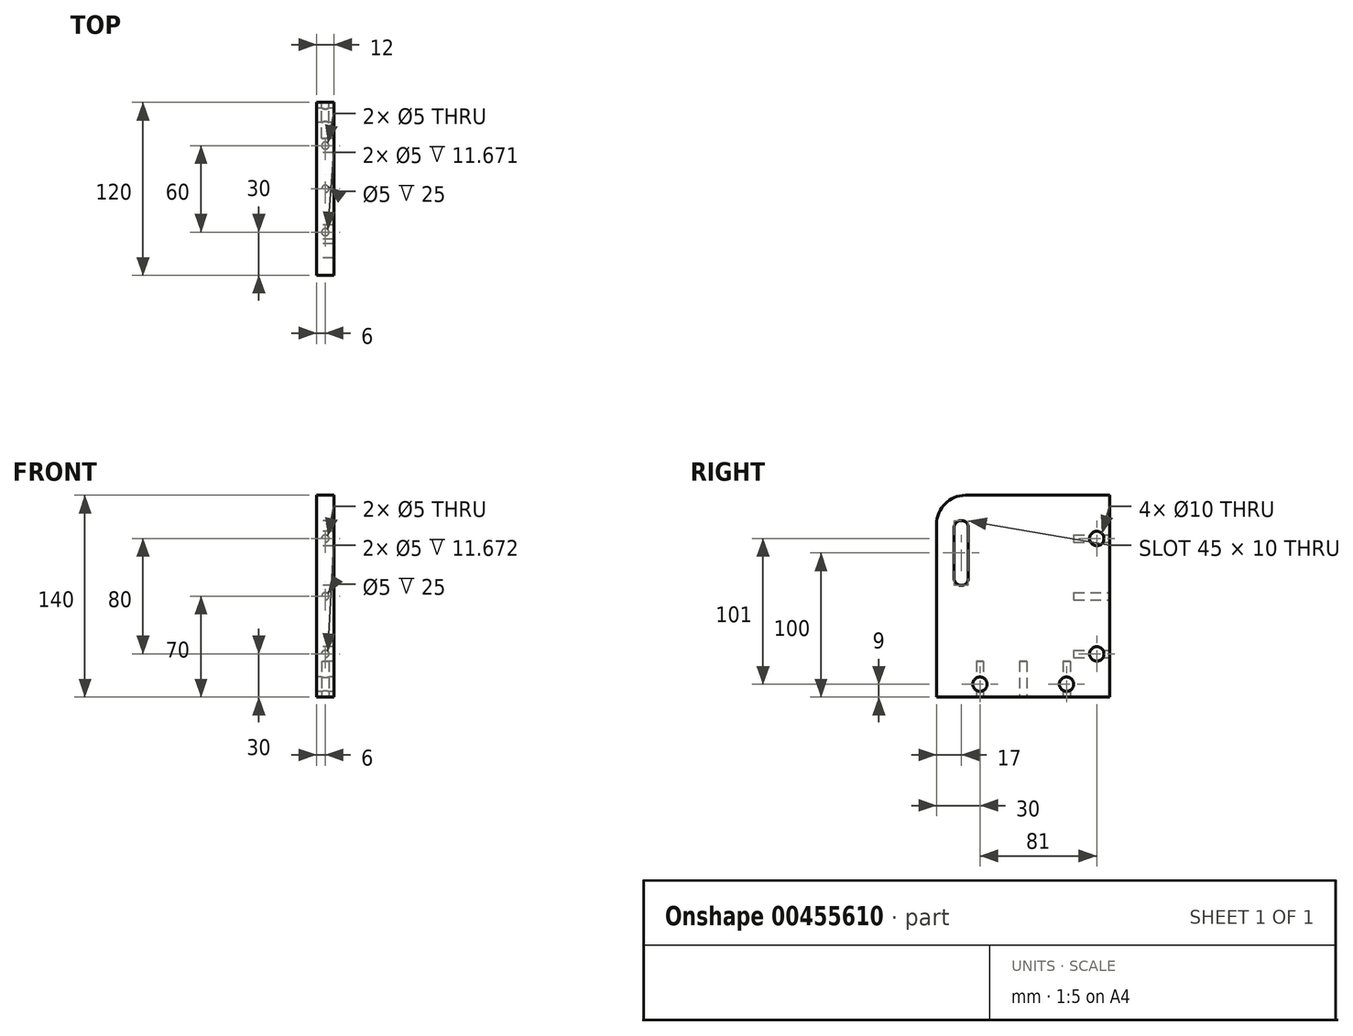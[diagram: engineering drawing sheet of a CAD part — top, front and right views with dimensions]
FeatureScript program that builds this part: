
annotation { "Feature Type Name" : "Feature", "Feature Type Description" : "" }
export const myFeature = defineFeature(function(context is Context, id is Id, definition is map)
    precondition{}
    {
        {
            var Q0;
            Q0=qCreatedBy(makeId("Right.planeOp"),FACE);
            var sketch = newSketch(context, id + "F0", { "sketchPlane" : qUnion([Q0])});
            skLineSegment(sketch, "E0.bottom", {"start": v(-60, 0) * mm, "end": v(60, 0) * mm});
            skLineSegment(sketch, "E0.top", {"start": v(-40, 140) * mm, "end": v(60, 140) * mm});
            skLineSegment(sketch, "E0.left", {"start": v(-60, 0) * mm, "end": v(-60, 120) * mm});
            skLineSegment(sketch, "E0.right", {"start": v(60, 0) * mm, "end": v(60, 140) * mm});
            skLineSegment(sketch, "E1.0", {"start": v(-60, 9) * mm, "end": v(60, 9) * mm, "construction": true});
            skLineSegment(sketch, "E2.0", {"start": v(51, 0) * mm, "end": v(51, 140) * mm, "construction": true});
            skCircle(sketch, "E3", {"center": v(51, 110) * mm, "radius": 5 * mm});
            skCircle(sketch, "E4", {"center": v(51, 30) * mm, "radius": 5 * mm});
            skCircle(sketch, "E5", {"center": v(-30, 9) * mm, "radius": 5 * mm});
            skCircle(sketch, "E6", {"center": v(30, 9) * mm, "radius": 5 * mm});
            skPoint(sketch, "E7.visualSharp", {"position": v(-60, 140) * mm});
            skArc(sketch, "E7.filletArc", {"start": v(-40, 140) * mm, "mid": v(-54.14, 134.14) * mm, "end": v(-60, 120) * mm});
            skLineSegment(sketch, "E8.bottom", {"start": v(-43, 122.5) * mm, "end": v(-43, 122.5) * mm});
            skLineSegment(sketch, "E8.top", {"start": v(-43, 77.5) * mm, "end": v(-43, 77.5) * mm});
            skLineSegment(sketch, "E8.left", {"start": v(-48, 117.5) * mm, "end": v(-48, 82.5) * mm});
            skLineSegment(sketch, "E8.right", {"start": v(-38, 117.5) * mm, "end": v(-38, 82.5) * mm});
            skPoint(sketch, "E9.visualSharp", {"position": v(-48, 122.5) * mm});
            skArc(sketch, "E9.filletArc", {"start": v(-43, 122.5) * mm, "mid": v(-46.54, 121.04) * mm, "end": v(-48, 117.5) * mm});
            skPoint(sketch, "E10.visualSharp", {"position": v(-38, 122.5) * mm});
            skArc(sketch, "E10.filletArc", {"start": v(-38, 117.5) * mm, "mid": v(-39.46, 121.04) * mm, "end": v(-43, 122.5) * mm});
            skPoint(sketch, "E11.visualSharp", {"position": v(-38, 77.5) * mm});
            skArc(sketch, "E11.filletArc", {"start": v(-43, 77.5) * mm, "mid": v(-39.46, 78.96) * mm, "end": v(-38, 82.5) * mm});
            skPoint(sketch, "E12.visualSharp", {"position": v(-48, 77.5) * mm});
            skArc(sketch, "E12.filletArc", {"start": v(-48, 82.5) * mm, "mid": v(-46.54, 78.96) * mm, "end": v(-43, 77.5) * mm});
            skPoint(sketch, "E13", {"position": v(-48, 100) * mm});
            skSolve(sketch);
        }
        {
            var Q0;
            Q0 = qSketchRegion(id + "F0", true);
            extrude(context, id + "F1", {"entities" : qUnion([Q0]), "depth" : 12 * mm});
        }
        {
            var Q0;
            Q0=makeQuery(id+"F1.opExtrude","SWEPT_FACE",FACE,{"disambiguationData":[OSD([sQuery(id+"F0.wireOp",EDGE,"E0.bottom")])]});
            var sketch = newSketch(context, id + "F2", { "sketchPlane" : qUnion([Q0])});
            skLineSegment(sketch, "E14", {"start": v(6, 60) * mm, "end": v(6, -60) * mm, "construction": true});
            skCircle(sketch, "E15", {"center": v(6, 0) * mm, "radius": 2.5 * mm});
            skCircle(sketch, "E16", {"center": v(6, 30) * mm, "radius": 2.5 * mm});
            skCircle(sketch, "E17", {"center": v(6, -30) * mm, "radius": 2.5 * mm});
            skSolve(sketch);
        }
        {
            var Q0;
            Q0 = qSketchRegion(id + "F2", true);
            extrude(context, id + "F3", {"entities" : qUnion([Q0]), "operationType" : NewBodyOperationType.REMOVE, "oppositeDirection" : true, "depth" : 25 * mm});
        }
        {
            var Q0;
            Q0=makeQuery(id+"F1.opExtrude","SWEPT_FACE",FACE,{"disambiguationData":[OSD([sQuery(id+"F0.wireOp",EDGE,"E0.right")])]});
            var sketch = newSketch(context, id + "F4", { "sketchPlane" : qUnion([Q0])});
            skLineSegment(sketch, "E18", {"start": v(-6, 0) * mm, "end": v(-6, 140) * mm, "construction": true});
            skCircle(sketch, "E19", {"center": v(-6, 70) * mm, "radius": 2.5 * mm});
            skCircle(sketch, "E20", {"center": v(-6, 110) * mm, "radius": 2.5 * mm});
            skCircle(sketch, "E21", {"center": v(-6, 30) * mm, "radius": 2.5 * mm});
            skSolve(sketch);
        }
        {
            var Q0;
            Q0 = qSketchRegion(id + "F4", true);
            extrude(context, id + "F5", {"entities" : qUnion([Q0]), "operationType" : NewBodyOperationType.REMOVE, "oppositeDirection" : true, "depth" : 25 * mm});
        }
    });
